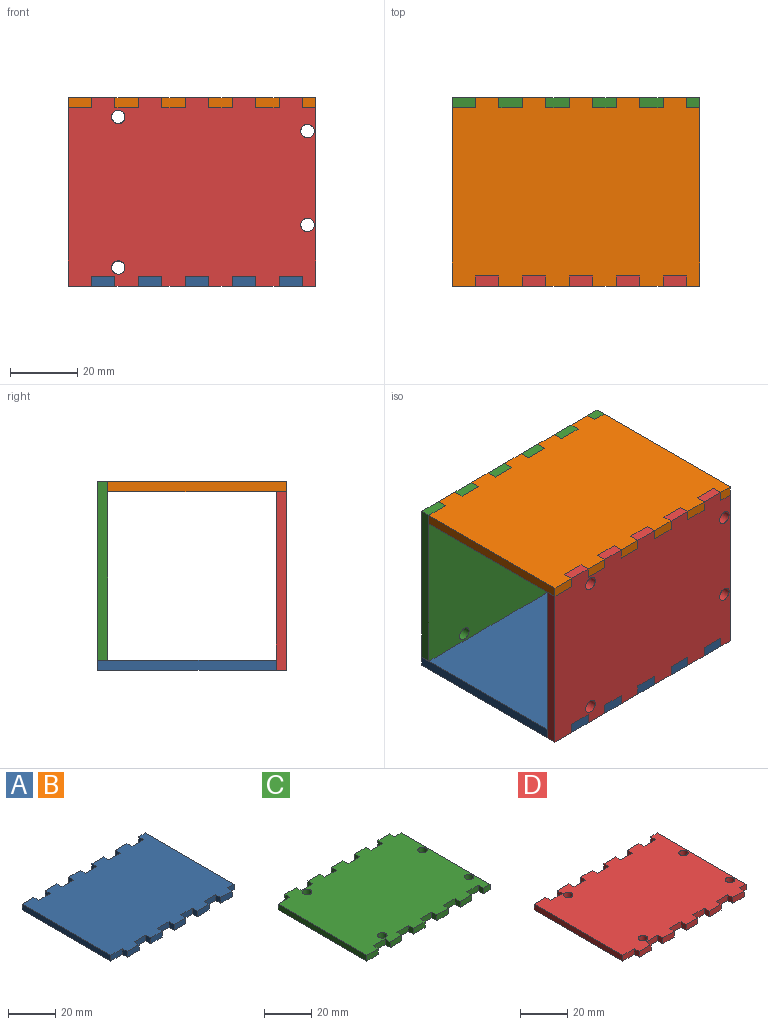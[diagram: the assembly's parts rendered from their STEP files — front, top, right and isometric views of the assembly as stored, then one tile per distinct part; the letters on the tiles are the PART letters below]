
ASSEMBLY  parts=4 mates=4
PART A: 46 faces, bbox 74x56.2x3 mm
  f0: plane 53.25x3mm, normal (-1,0,0), area 159.7mm2, adj f1,f43,f44,f45
  f1: plane 7x3mm, normal (0,-1,0), area 21mm2, adj f0,f2,f44,f45
  f2: plane 3x3mm, normal (-1,0,0), area 9mm2, adj f1,f3,f44,f45
  f3: plane 7x3mm, normal (0,-1,0), area 21mm2, adj f2,f4,f44,f45
  f4: plane 3x3mm, normal (1,0,0), area 9mm2, adj f3,f5,f44,f45
  f5: plane 7x3mm, normal (0,-1,0), area 21mm2, adj f4,f6,f44,f45
  f6: plane 3x3mm, normal (-1,0,0), area 9mm2, adj f5,f7,f44,f45
  f7: plane 7x3mm, normal (0,-1,0), area 21mm2, adj f6,f8,f44,f45
  f8: plane 3x3mm, normal (1,0,0), area 9mm2, adj f7,f9,f44,f45
  f9: plane 7x3mm, normal (0,-1,0), area 21mm2, adj f8,f10,f44,f45
  f10: plane 3x3mm, normal (-1,0,0), area 9mm2, adj f9,f11,f44,f45
  f11: plane 7x3mm, normal (0,-1,0), area 21mm2, adj f10,f12,f44,f45
  f12: plane 3x3mm, normal (1,0,0), area 9mm2, adj f11,f13,f44,f45
  f13: plane 7x3mm, normal (0,-1,0), area 21mm2, adj f12,f14,f44,f45
  f14: plane 3x3mm, normal (-1,0,0), area 9mm2, adj f13,f15,f44,f45
  f15: plane 7x3mm, normal (0,-1,0), area 21mm2, adj f14,f16,f44,f45
  f16: plane 3x3mm, normal (1,0,0), area 9mm2, adj f15,f17,f44,f45
  f17: plane 7x3mm, normal (0,-1,0), area 21mm2, adj f16,f18,f44,f45
  f18: plane 3x3mm, normal (-1,0,0), area 9mm2, adj f17,f19,f44,f45
  f19: plane 7x3mm, normal (0,-1,0), area 21mm2, adj f18,f20,f44,f45
  f20: plane 3x3mm, normal (1,0,0), area 9mm2, adj f19,f21,f44,f45
  f21: plane 4x3mm, normal (0,-1,0), area 12mm2, adj f20,f22,f44,f45
  f22: plane 53.25x3mm, normal (1,0,0), area 159.7mm2, adj f21,f23,f44,f45
  f23: plane 4x3mm, normal (0,1,0), area 12mm2, adj f22,f24,f44,f45
  f24: plane 3x3mm, normal (-1,0,0), area 9mm2, adj f23,f25,f44,f45
  f25: plane 7x3mm, normal (0,1,0), area 21mm2, adj f24,f26,f44,f45
  f26: plane 3x3mm, normal (1,0,0), area 9mm2, adj f25,f27,f44,f45
  f27: plane 7x3mm, normal (0,1,0), area 21mm2, adj f26,f28,f44,f45
  f28: plane 3x3mm, normal (-1,0,0), area 9mm2, adj f27,f29,f44,f45
  f29: plane 7x3mm, normal (0,1,0), area 21mm2, adj f28,f30,f44,f45
  f30: plane 3x3mm, normal (1,0,0), area 9mm2, adj f29,f31,f44,f45
  f31: plane 7x3mm, normal (0,1,0), area 21mm2, adj f30,f32,f44,f45
  f32: plane 3x3mm, normal (-1,0,0), area 9mm2, adj f31,f33,f44,f45
  f33: plane 7x3mm, normal (0,1,0), area 21mm2, adj f32,f34,f44,f45
  f34: plane 3x3mm, normal (1,0,0), area 9mm2, adj f33,f35,f44,f45
  f35: plane 7x3mm, normal (0,1,0), area 21mm2, adj f34,f36,f44,f45
  f36: plane 3x3mm, normal (-1,0,0), area 9mm2, adj f35,f37,f44,f45
  f37: plane 7x3mm, normal (0,1,0), area 21mm2, adj f36,f38,f44,f45
  f38: plane 3x3mm, normal (1,0,0), area 9mm2, adj f37,f39,f44,f45
  f39: plane 7x3mm, normal (0,1,0), area 21mm2, adj f38,f40,f44,f45
  f40: plane 3x3mm, normal (-1,0,0), area 9mm2, adj f39,f41,f44,f45
  f41: plane 7x3mm, normal (0,1,0), area 21mm2, adj f40,f42,f44,f45
  f42: plane 3x3mm, normal (1,0,0), area 9mm2, adj f41,f43,f44,f45
  f43: plane 7x3mm, normal (0,1,0), area 21mm2, adj f0,f42,f44,f45
  f44: plane 74x56.25mm, normal (0,0,1), area 3940.1mm2, adj f0,f1,f2,f3,f4,f5,f6,f7
  f45: plane 74x56.25mm, normal (0,0,-1), area 3940.1mm2, adj f0,f1,f2,f3,f4,f5,f6,f7
PART B: same geometry as A
PART C: 50 faces, bbox 74x56.4x3 mm
  f0: plane 74x56.35mm, normal (0,0,1), area 3897.6mm2, adj f2,f3,f4,f5,f6,f7,f8,f9
  f1: plane 74x56.35mm, normal (0,0,-1), area 3897.6mm2, adj f2,f3,f4,f5,f6,f7,f8,f9
  f2: plane 53.35x3mm, normal (-1,0,0), area 160mm2, adj f0,f1,f3,f45
  f3: plane 7x3mm, normal (0,-1,0), area 21mm2, adj f0,f1,f2,f4
  f4: plane 3x3mm, normal (1,0,0), area 9mm2, adj f0,f1,f3,f5
  f5: plane 7x3mm, normal (0,-1,0), area 21mm2, adj f0,f1,f4,f6
  f6: plane 3x3mm, normal (-1,0,0), area 9mm2, adj f0,f1,f5,f7
  f7: plane 7x3mm, normal (0,-1,0), area 21mm2, adj f0,f1,f6,f8
  f8: plane 3x3mm, normal (1,0,0), area 9mm2, adj f0,f1,f7,f9
  f9: plane 7x3mm, normal (0,-1,0), area 21mm2, adj f0,f1,f8,f10
  f10: plane 3x3mm, normal (-1,0,0), area 9mm2, adj f0,f1,f9,f11
  f11: plane 7x3mm, normal (0,-1,0), area 21mm2, adj f0,f1,f10,f12
  f12: plane 3x3mm, normal (1,0,0), area 9mm2, adj f0,f1,f11,f13
  f13: plane 7x3mm, normal (0,-1,0), area 21mm2, adj f0,f1,f12,f14
  f14: plane 3x3mm, normal (-1,0,0), area 9mm2, adj f0,f1,f13,f15
  f15: plane 7x3mm, normal (0,-1,0), area 21mm2, adj f0,f1,f14,f16
  f16: plane 3x3mm, normal (1,0,0), area 9mm2, adj f0,f1,f15,f17
  f17: plane 7x3mm, normal (0,-1,0), area 21mm2, adj f0,f1,f16,f18
  f18: plane 3x3mm, normal (-1,0,0), area 9mm2, adj f0,f1,f17,f19
  f19: plane 7x3mm, normal (0,-1,0), area 21mm2, adj f0,f1,f18,f20
  f20: plane 3x3mm, normal (1,0,0), area 9mm2, adj f0,f1,f19,f21
  f21: plane 7x3mm, normal (0,-1,0), area 21mm2, adj f0,f1,f20,f22
  f22: plane 3x3mm, normal (-1,0,0), area 9mm2, adj f0,f1,f21,f23
  f23: plane 4x3mm, normal (0,-1,0), area 12mm2, adj f0,f1,f22,f24
  f24: plane 53.35x3mm, normal (1,0,0), area 160mm2, adj f0,f1,f23,f25
  f25: plane 4x3mm, normal (0,1,0), area 12mm2, adj f0,f1,f24,f26
  f26: plane 3x3mm, normal (1,0,0), area 9mm2, adj f0,f1,f25,f27
  f27: plane 7x3mm, normal (0,1,0), area 21mm2, adj f0,f1,f26,f28
  f28: plane 3x3mm, normal (-1,0,0), area 9mm2, adj f0,f1,f27,f29
  f29: plane 7x3mm, normal (0,1,0), area 21mm2, adj f0,f1,f28,f30
  f30: plane 3x3mm, normal (1,0,0), area 9mm2, adj f0,f1,f29,f31
  f31: plane 7x3mm, normal (0,1,0), area 21mm2, adj f0,f1,f30,f32
  f32: plane 3x3mm, normal (-1,0,0), area 9mm2, adj f0,f1,f31,f33
  f33: plane 7x3mm, normal (0,1,0), area 21mm2, adj f0,f1,f32,f34
  f34: plane 3x3mm, normal (1,0,0), area 9mm2, adj f0,f1,f33,f35
  f35: plane 7x3mm, normal (0,1,0), area 21mm2, adj f0,f1,f34,f36
  f36: plane 3x3mm, normal (-1,0,0), area 9mm2, adj f0,f1,f35,f37
  f37: plane 7x3mm, normal (0,1,0), area 21mm2, adj f0,f1,f36,f38
  f38: plane 3x3mm, normal (1,0,0), area 9mm2, adj f0,f1,f37,f39
  f39: plane 7x3mm, normal (0,1,0), area 21mm2, adj f0,f1,f38,f40
  f40: plane 3x3mm, normal (-1,0,0), area 9mm2, adj f0,f1,f39,f41
  f41: plane 7x3mm, normal (0,1,0), area 21mm2, adj f0,f1,f40,f42
  f42: plane 3x3mm, normal (1,0,0), area 9mm2, adj f0,f1,f41,f43
  f43: plane 7x3mm, normal (0,1,0), area 21mm2, adj f0,f1,f42,f44
  f44: plane 3x3mm, normal (-1,0,0), area 9mm2, adj f0,f1,f43,f45
  f45: plane 7x3mm, normal (0,1,0), area 21mm2, adj f0,f1,f2,f44
  f46: cylinder r=2mm len=4mm, axis (0,0,1), area 37.7mm2, adj f0,f1
  f47: cylinder r=2mm len=4mm, axis (0,0,1), area 37.7mm2, adj f0,f1
  f48: cylinder r=2mm len=4mm, axis (0,0,1), area 37.7mm2, adj f0,f1
  f49: cylinder r=2mm len=4mm, axis (0,0,1), area 37.7mm2, adj f0,f1
PART D: 50 faces, bbox 74x56.3x3 mm
  f0: plane 74x56.25mm, normal (0,0,1), area 3890.2mm2, adj f2,f3,f4,f5,f6,f7,f8,f9
  f1: plane 74x56.25mm, normal (0,0,-1), area 3890.2mm2, adj f2,f3,f4,f5,f6,f7,f8,f9
  f2: plane 7x3mm, normal (0,-1,0), area 21mm2, adj f0,f1,f3,f45
  f3: plane 3x3mm, normal (1,0,0), area 9mm2, adj f0,f1,f2,f4
  f4: plane 7x3mm, normal (0,-1,0), area 21mm2, adj f0,f1,f3,f5
  f5: plane 3x3mm, normal (-1,0,0), area 9mm2, adj f0,f1,f4,f6
  f6: plane 7x3mm, normal (0,-1,0), area 21mm2, adj f0,f1,f5,f7
  f7: plane 3x3mm, normal (1,0,0), area 9mm2, adj f0,f1,f6,f8
  f8: plane 7x3mm, normal (0,-1,0), area 21mm2, adj f0,f1,f7,f9
  f9: plane 3x3mm, normal (-1,0,0), area 9mm2, adj f0,f1,f8,f10
  f10: plane 7x3mm, normal (0,-1,0), area 21mm2, adj f0,f1,f9,f11
  f11: plane 3x3mm, normal (1,0,0), area 9mm2, adj f0,f1,f10,f12
  f12: plane 7x3mm, normal (0,-1,0), area 21mm2, adj f0,f1,f11,f13
  f13: plane 3x3mm, normal (-1,0,0), area 9mm2, adj f0,f1,f12,f14
  f14: plane 7x3mm, normal (0,-1,0), area 21mm2, adj f0,f1,f13,f15
  f15: plane 3x3mm, normal (1,0,0), area 9mm2, adj f0,f1,f14,f16
  f16: plane 7x3mm, normal (0,-1,0), area 21mm2, adj f0,f1,f15,f17
  f17: plane 3x3mm, normal (-1,0,0), area 9mm2, adj f0,f1,f16,f18
  f18: plane 7x3mm, normal (0,-1,0), area 21mm2, adj f0,f1,f17,f19
  f19: plane 3x3mm, normal (1,0,0), area 9mm2, adj f0,f1,f18,f20
  f20: plane 4x3mm, normal (0,-1,0), area 12mm2, adj f0,f1,f19,f21
  f21: plane 53.25x3mm, normal (1,0,0), area 159.7mm2, adj f0,f1,f20,f22
  f22: plane 4x3mm, normal (0,1,0), area 12mm2, adj f0,f1,f21,f23
  f23: plane 3x3mm, normal (-1,0,0), area 9mm2, adj f0,f1,f22,f24
  f24: plane 7x3mm, normal (0,1,0), area 21mm2, adj f0,f1,f23,f25
  f25: plane 3x3mm, normal (1,0,0), area 9mm2, adj f0,f1,f24,f26
  f26: plane 7x3mm, normal (0,1,0), area 21mm2, adj f0,f1,f25,f27
  f27: plane 3x3mm, normal (-1,0,0), area 9mm2, adj f0,f1,f26,f28
  f28: plane 7x3mm, normal (0,1,0), area 21mm2, adj f0,f1,f27,f29
  f29: plane 3x3mm, normal (1,0,0), area 9mm2, adj f0,f1,f28,f30
  f30: plane 7x3mm, normal (0,1,0), area 21mm2, adj f0,f1,f29,f31
  f31: plane 3x3mm, normal (-1,0,0), area 9mm2, adj f0,f1,f30,f32
  f32: plane 7x3mm, normal (0,1,0), area 21mm2, adj f0,f1,f31,f33
  f33: plane 3x3mm, normal (1,0,0), area 9mm2, adj f0,f1,f32,f34
  f34: plane 7x3mm, normal (0,1,0), area 21mm2, adj f0,f1,f33,f35
  f35: plane 3x3mm, normal (-1,0,0), area 9mm2, adj f0,f1,f34,f36
  f36: plane 7x3mm, normal (0,1,0), area 21mm2, adj f0,f1,f35,f37
  f37: plane 3x3mm, normal (1,0,0), area 9mm2, adj f0,f1,f36,f38
  f38: plane 7x3mm, normal (0,1,0), area 21mm2, adj f0,f1,f37,f39
  f39: plane 3x3mm, normal (-1,0,0), area 9mm2, adj f0,f1,f38,f40
  f40: plane 7x3mm, normal (0,1,0), area 21mm2, adj f0,f1,f39,f41
  f41: plane 3x3mm, normal (1,0,0), area 9mm2, adj f0,f1,f40,f42
  f42: plane 7x3mm, normal (0,1,0), area 21mm2, adj f0,f1,f41,f43
  f43: plane 53.25x3mm, normal (-1,0,0), area 159.7mm2, adj f0,f1,f42,f44
  f44: plane 7x3mm, normal (0,-1,0), area 21mm2, adj f0,f1,f43,f45
  f45: plane 3x3mm, normal (-1,0,0), area 9mm2, adj f0,f1,f2,f44
  f46: cylinder r=2mm len=4mm, axis (0,0,1), area 37.7mm2, adj f0,f1
  f47: cylinder r=2mm len=4mm, axis (0,0,1), area 37.7mm2, adj f0,f1
  f48: cylinder r=2mm len=4mm, axis (0,0,1), area 37.7mm2, adj f0,f1
  f49: cylinder r=2mm len=4mm, axis (0,0,1), area 37.7mm2, adj f0,f1
PLACE A t=(413.25,169.56,-487.35)mm
PLACE B rot(axis=(-1,0,0),180deg) t=(413.25,169.31,-431.1)mm
PLACE C rot(axis=(-1,0,0),90deg) t=(413.25,-97.64,-459.35)mm
PLACE D rot(axis=(-1,0,0),90deg) t=(413.25,44.31,-459.35)mm
MATE parallel C.f22 <-> B.f20  axis (-1,0,0) through (446.25,196.06,-432.6)mm
MATE parallel B.f24 <-> D.f19  axis (-1,0,0) through (446.25,142.81,-432.6)mm
MATE parallel D.f23 <-> A.f20  axis (-1,0,0) through (446.25,142.81,-485.85)mm
MATE parallel D.f23 <-> A.f20  axis (-1,0,0) through (446.25,142.81,-485.85)mm
